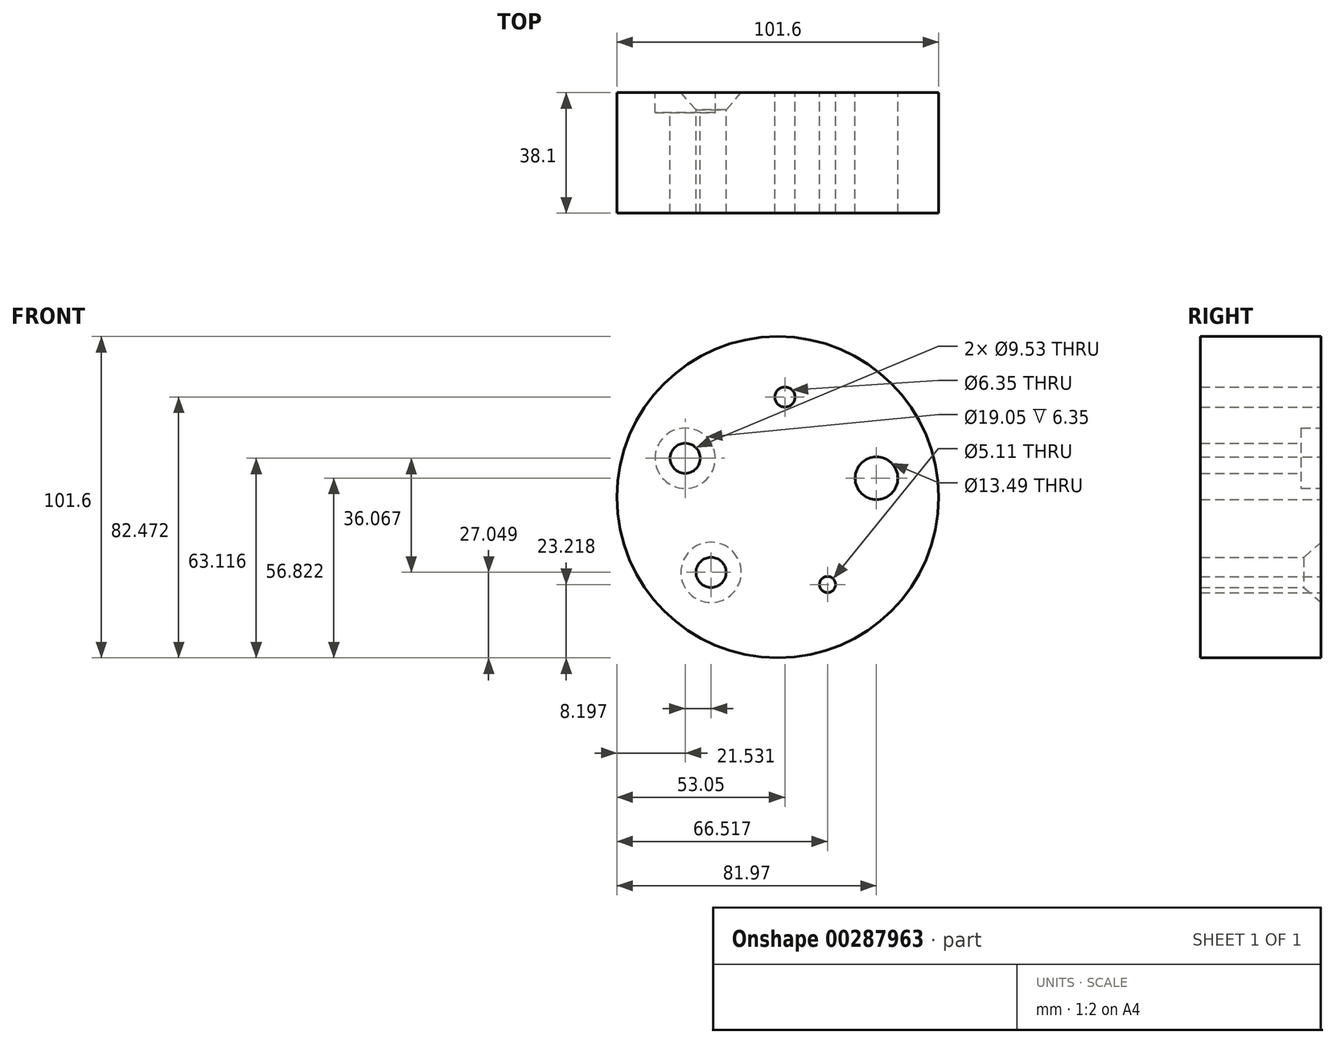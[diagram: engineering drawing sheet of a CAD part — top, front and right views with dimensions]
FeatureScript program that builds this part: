
annotation { "Feature Type Name" : "Feature", "Feature Type Description" : "" }
export const myFeature = defineFeature(function(context is Context, id is Id, definition is map)
    precondition{}
    {
        {
            var Q0;
            Q0=qCreatedBy(makeId("Front.planeOp"),FACE);
            var sketch = newSketch(context, id + "F0", { "sketchPlane" : qUnion([Q0])});
            skCircle(sketch, "E0", {"center": v(-69.18, 39.43) * mm, "radius": 50.8 * mm});
            skCircle(sketch, "E1", {"center": v(-69.18, 39.43) * mm, "radius": 31.75 * mm});
            skPoint(sketch, "E2", {"position": v(-66.93, 71.1) * mm});
            skPoint(sketch, "E3.1.0", {"position": v(-98.45, 51.75) * mm});
            skPoint(sketch, "E3.2.0", {"position": v(-90.25, 15.68) * mm});
            skPoint(sketch, "E3.3.0", {"position": v(-53.46, 11.85) * mm});
            skPoint(sketch, "E3.4.0", {"position": v(-38, 45.45) * mm});
            skLineSegment(sketch, "E3.anchor1", {"start": v(-69.18, 39.43) * mm, "end": v(-66.93, 71.1) * mm, "construction": true});
            skLineSegment(sketch, "E3.anchor2", {"start": v(-69.18, 39.43) * mm, "end": v(-38, 45.45) * mm, "construction": true});
            skSolve(sketch);
        }
        {
            var Q0;
            Q0=makeQuery(id+"F0.imprint","IMPRINT",FACE,{"disambiguationData":[TD([[makeQuery(id+"F0.imprint","IMPRINT",EDGE,{"derivedFrom":sQuery(id+"F0.wireOp",EDGE,"E0")}),1.0]])]});
            var Q1;
            Q1=makeQuery(id+"F0.imprint","IMPRINT",FACE,{"disambiguationData":[TD([[makeQuery(id+"F0.imprint","IMPRINT",EDGE,{"derivedFrom":sQuery(id+"F0.wireOp",EDGE,"E1")}),1.0]])]});
            extrude(context, id + "F1", {"entities" : qUnion([Q0, Q1]), "depth" : 38.1 * mm});
        }
        {
            var Q0;
            Q0=sQuery(id+"F0.wireOp",VERTEX,"E2");
            var Q1;
            Q1=makeQuery(id+"F1.opExtrude","SWEPT_BODY",BODY,{"disambiguationData":[OSD([sQuery(id+"F0.wireOp",EDGE,"E0")])]});
            hole(context, id + "F2", {"style" : HoleStyle.SIMPLE, "endStyle" : HoleEndStyle.THROUGH, "oppositeDirection" : true, "holeDiameter" : 6.35 * mm, "isTappedThrough" : true, "tappedDepth" : 12.7 * mm, "tapClearance" : 3, "locations" : qUnion([Q0]), "scope" : qUnion([Q1])});
        }
        {
            var Q0;
            Q0=sQuery(id+"F0.wireOp",VERTEX,"E3.1.0");
            var Q1;
            Q1=makeQuery(id+"F1.opExtrude","SWEPT_BODY",BODY,{"disambiguationData":[OSD([sQuery(id+"F0.wireOp",EDGE,"E0")])]});
            hole(context, id + "F3", {"style" : HoleStyle.C_BORE, "endStyle" : HoleEndStyle.THROUGH, "oppositeDirection" : true, "holeDiameter" : 9.52 * mm, "cBoreDiameter" : 19.05 * mm, "cBoreDepth" : 6.35 * mm, "isTappedThrough" : true, "tappedDepth" : 12.7 * mm, "tapClearance" : 3, "locations" : qUnion([Q0]), "scope" : qUnion([Q1])});
        }
        {
            var Q0;
            Q0=sQuery(id+"F0.wireOp",VERTEX,"E3.2.0");
            var Q1;
            Q1=makeQuery(id+"F1.opExtrude","SWEPT_BODY",BODY,{"disambiguationData":[OSD([sQuery(id+"F0.wireOp",EDGE,"E0")])]});
            hole(context, id + "F4", {"style" : HoleStyle.C_SINK, "endStyle" : HoleEndStyle.THROUGH, "oppositeDirection" : true, "holeDiameter" : 9.52 * mm, "cSinkDiameter" : 19.05 * mm, "cSinkAngle" : 82 * degree, "isTappedThrough" : true, "tappedDepth" : 12.7 * mm, "tapClearance" : 3, "locations" : qUnion([Q0]), "scope" : qUnion([Q1])});
        }
        {
            var Q0;
            Q0=sQuery(id+"F0.wireOp",VERTEX,"E3.3.0");
            var Q1;
            Q1=makeQuery(id+"F1.opExtrude","SWEPT_BODY",BODY,{"disambiguationData":[OSD([sQuery(id+"F0.wireOp",EDGE,"E0")])]});
            hole(context, id + "F5", {"style" : HoleStyle.SIMPLE, "endStyle" : HoleEndStyle.THROUGH, "oppositeDirection" : true, "standardTappedOrClearance" : lookupTablePath({ "standard" : "ANSI", "engagement" : "75%", "pitch" : "20 tpi", "size" : "1/4", "type" : "Tapped" }), "standardBlindInLast" : lookupTablePath({ "standard" : "ANSI", "engagement" : "75%", "pitch" : "20 tpi", "size" : "1/4", "type" : "Tapped" }), "holeDiameter" : 5.1 * mm, "showTappedDepth" : true, "isTappedThrough" : true, "tappedDepth" : 12.7 * mm, "tapClearance" : 3, "locations" : qUnion([Q0]), "scope" : qUnion([Q1]), "majorDiameter" : 6.35 * mm});
        }
        {
            var Q0;
            Q0=sQuery(id+"F0.wireOp",VERTEX,"E3.4.0");
            var Q1;
            Q1=makeQuery(id+"F1.opExtrude","SWEPT_BODY",BODY,{"disambiguationData":[OSD([sQuery(id+"F0.wireOp",EDGE,"E0")])]});
            hole(context, id + "F6", {"style" : HoleStyle.SIMPLE, "endStyle" : HoleEndStyle.THROUGH, "oppositeDirection" : true, "holeDiameter" : 13.5 * mm, "isTappedThrough" : true, "tappedDepth" : 12.7 * mm, "tapClearance" : 3, "locations" : qUnion([Q0]), "scope" : qUnion([Q1])});
        }
    });
